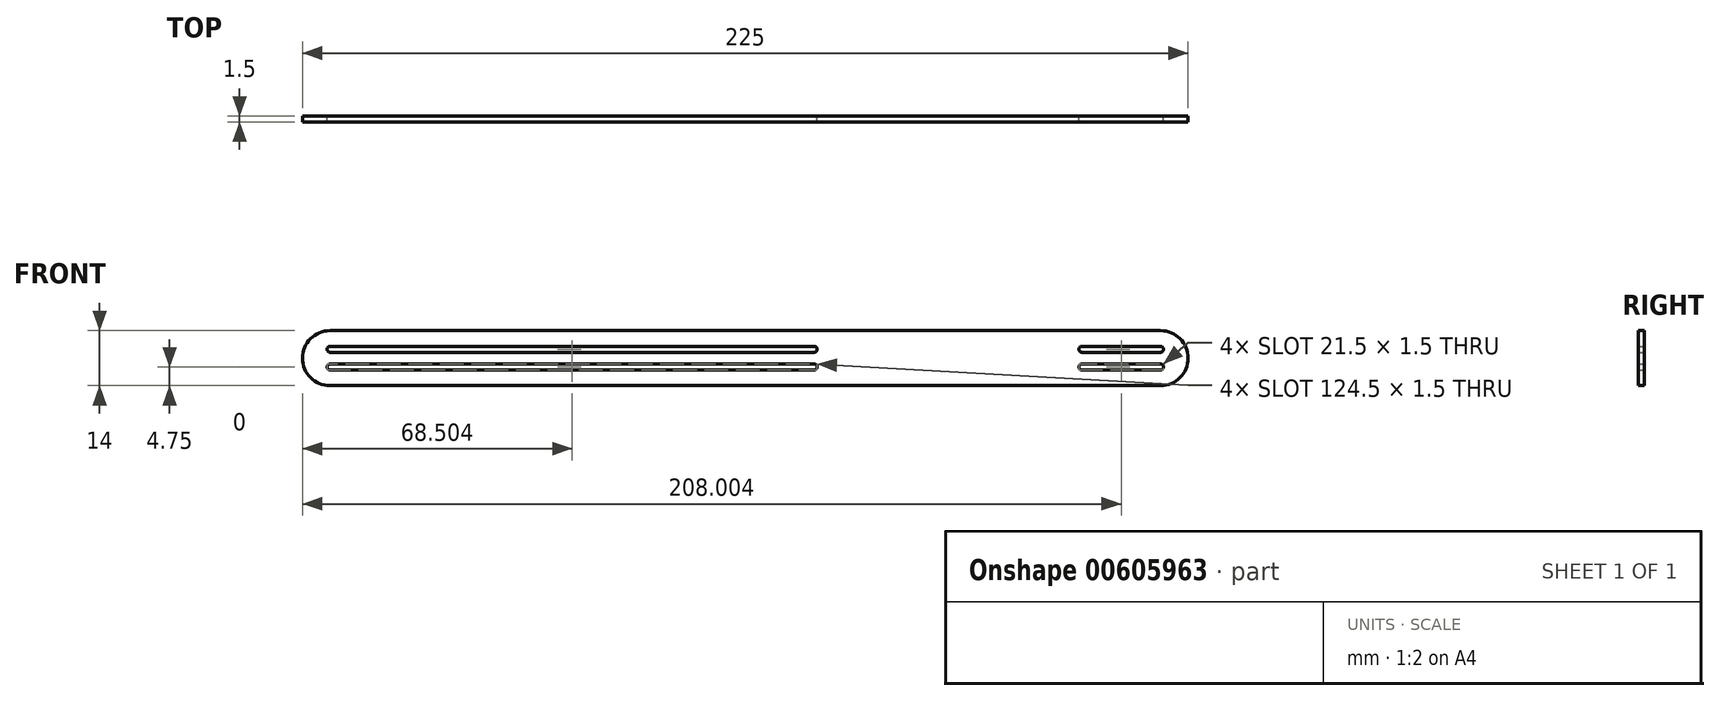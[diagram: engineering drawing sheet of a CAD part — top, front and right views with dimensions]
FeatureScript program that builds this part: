
annotation { "Feature Type Name" : "Feature", "Feature Type Description" : "" }
export const myFeature = defineFeature(function(context is Context, id is Id, definition is map)
    precondition{}
    {
        {
            var Q0;
            Q0=qCreatedBy(makeId("Front.planeOp"),FACE);
            var sketch = newSketch(context, id + "F0", { "sketchPlane" : qUnion([Q0])});
            skLineSegment(sketch, "E0.bottom", {"start": v(-136.23, 21.39) * mm, "end": v(74.77, 21.39) * mm});
            skLineSegment(sketch, "E0.top", {"start": v(-136.23, 7.39) * mm, "end": v(74.77, 7.39) * mm});
            skLineSegment(sketch, "E0.left", {"start": v(-136.23, 21.39) * mm, "end": v(-136.23, 7.39) * mm, "construction": true});
            skLineSegment(sketch, "E0.right", {"start": v(74.77, 21.39) * mm, "end": v(74.77, 7.39) * mm, "construction": true});
            skLineSegment(sketch, "E1", {"start": v(-136.23, 16.64) * mm, "end": v(-13.23, 16.64) * mm, "construction": true});
            skLineSegment(sketch, "E2", {"start": v(-136.23, 12.14) * mm, "end": v(-13.23, 12.14) * mm, "construction": true});
            skArc(sketch, "E3.0.startCap", {"start": v(-136.23, 15.89) * mm, "mid": v(-136.98, 16.64) * mm, "end": v(-136.23, 17.39) * mm});
            skArc(sketch, "E3.0.endCap", {"start": v(-13.23, 17.39) * mm, "mid": v(-12.48, 16.64) * mm, "end": v(-13.23, 15.89) * mm});
            skLineSegment(sketch, "E3.0.left", {"start": v(-136.23, 17.39) * mm, "end": v(-13.23, 17.39) * mm});
            skLineSegment(sketch, "E3.0.right", {"start": v(-136.23, 15.89) * mm, "end": v(-13.23, 15.89) * mm});
            skArc(sketch, "E4", {"start": v(-136.23, 21.39) * mm, "mid": v(-141.21, 19.3) * mm, "end": v(-143.23, 14.29) * mm});
            skArc(sketch, "E5", {"start": v(74.77, 21.39) * mm, "mid": v(79.8, 19.27) * mm, "end": v(81.77, 14.2) * mm});
            skArc(sketch, "E6.0.startCap", {"start": v(-136.23, 11.39) * mm, "mid": v(-136.98, 12.14) * mm, "end": v(-136.23, 12.89) * mm});
            skArc(sketch, "E6.0.endCap", {"start": v(-13.23, 12.89) * mm, "mid": v(-12.48, 12.14) * mm, "end": v(-13.23, 11.39) * mm});
            skLineSegment(sketch, "E6.0.left", {"start": v(-136.23, 12.89) * mm, "end": v(-13.23, 12.89) * mm});
            skLineSegment(sketch, "E6.0.right", {"start": v(-136.23, 11.39) * mm, "end": v(-13.23, 11.39) * mm});
            skLineSegment(sketch, "E7", {"start": v(74.77, 16.64) * mm, "end": v(54.77, 16.64) * mm, "construction": true});
            skLineSegment(sketch, "E8", {"start": v(74.77, 12.14) * mm, "end": v(54.77, 12.14) * mm, "construction": true});
            skArc(sketch, "E9.0.startCap", {"start": v(74.77, 12.89) * mm, "mid": v(75.52, 12.14) * mm, "end": v(74.77, 11.39) * mm});
            skArc(sketch, "E9.0.endCap", {"start": v(54.77, 11.39) * mm, "mid": v(54.02, 12.14) * mm, "end": v(54.77, 12.89) * mm});
            skLineSegment(sketch, "E9.0.left", {"start": v(74.77, 11.39) * mm, "end": v(54.77, 11.39) * mm});
            skLineSegment(sketch, "E9.0.right", {"start": v(74.77, 12.89) * mm, "end": v(54.77, 12.89) * mm});
            skArc(sketch, "E9.1.startCap", {"start": v(74.77, 17.39) * mm, "mid": v(75.52, 16.64) * mm, "end": v(74.77, 15.89) * mm});
            skArc(sketch, "E9.1.endCap", {"start": v(54.77, 15.89) * mm, "mid": v(54.02, 16.64) * mm, "end": v(54.77, 17.39) * mm});
            skLineSegment(sketch, "E9.1.left", {"start": v(74.77, 15.89) * mm, "end": v(54.77, 15.89) * mm});
            skLineSegment(sketch, "E9.1.right", {"start": v(74.77, 17.39) * mm, "end": v(54.77, 17.39) * mm});
            skLineSegment(sketch, "E10", {"start": v(-97.23, -33.2) * mm, "end": v(73.77, -33.2) * mm, "construction": true});
            skArc(sketch, "E11.0.startCap", {"start": v(-97.23, -41.2) * mm, "mid": v(-102.9, -38.83) * mm, "end": v(-105.23, -33.14) * mm});
            skArc(sketch, "E11.0.endCap", {"start": v(73.77, -25.2) * mm, "mid": v(79.34, -27.45) * mm, "end": v(81.77, -32.94) * mm});
            skLineSegment(sketch, "E11.0.left", {"start": v(-97.23, -25.2) * mm, "end": v(73.77, -25.2) * mm});
            skLineSegment(sketch, "E11.0.right", {"start": v(-97.23, -41.2) * mm, "end": v(73.77, -41.2) * mm});
            skLineSegment(sketch, "E12", {"start": v(-97.23, -25.2) * mm, "end": v(-97.23, -41.2) * mm, "construction": true});
            skLineSegment(sketch, "E13", {"start": v(73.77, -25.2) * mm, "end": v(73.77, -41.2) * mm, "construction": true});
            skLineSegment(sketch, "E14", {"start": v(-97.23, -36.44) * mm, "end": v(-17.23, -36.44) * mm, "construction": true});
            skLineSegment(sketch, "E15", {"start": v(-97.23, -29.94) * mm, "end": v(-17.23, -29.94) * mm, "construction": true});
            skLineSegment(sketch, "E16", {"start": v(73.77, -36.44) * mm, "end": v(53.77, -36.44) * mm, "construction": true});
            skLineSegment(sketch, "E17", {"start": v(73.77, -29.99) * mm, "end": v(53.77, -29.99) * mm, "construction": true});
            skArc(sketch, "E18.0.startCap", {"start": v(-97.23, -37.2) * mm, "mid": v(-97.98, -36.44) * mm, "end": v(-97.23, -35.7) * mm});
            skArc(sketch, "E18.0.endCap", {"start": v(-17.23, -35.7) * mm, "mid": v(-16.48, -36.44) * mm, "end": v(-17.23, -37.2) * mm});
            skLineSegment(sketch, "E18.0.left", {"start": v(-97.23, -35.7) * mm, "end": v(-17.23, -35.7) * mm});
            skLineSegment(sketch, "E18.0.right", {"start": v(-97.23, -37.2) * mm, "end": v(-17.23, -37.2) * mm});
            skArc(sketch, "E18.1.startCap", {"start": v(-97.23, -30.7) * mm, "mid": v(-97.98, -29.94) * mm, "end": v(-97.23, -29.2) * mm});
            skArc(sketch, "E18.1.endCap", {"start": v(-17.23, -29.2) * mm, "mid": v(-16.48, -29.94) * mm, "end": v(-17.23, -30.7) * mm});
            skLineSegment(sketch, "E18.1.left", {"start": v(-97.23, -29.2) * mm, "end": v(-17.23, -29.2) * mm});
            skLineSegment(sketch, "E18.1.right", {"start": v(-97.23, -30.7) * mm, "end": v(-17.23, -30.7) * mm});
            skArc(sketch, "E18.2.startCap", {"start": v(73.77, -29.24) * mm, "mid": v(74.52, -29.99) * mm, "end": v(73.77, -30.74) * mm});
            skArc(sketch, "E18.2.endCap", {"start": v(53.77, -30.74) * mm, "mid": v(53.02, -29.99) * mm, "end": v(53.77, -29.24) * mm});
            skLineSegment(sketch, "E18.2.left", {"start": v(73.77, -30.74) * mm, "end": v(53.77, -30.74) * mm});
            skLineSegment(sketch, "E18.2.right", {"start": v(73.77, -29.24) * mm, "end": v(53.77, -29.24) * mm});
            skArc(sketch, "E18.3.startCap", {"start": v(73.77, -35.7) * mm, "mid": v(74.52, -36.44) * mm, "end": v(73.77, -37.2) * mm});
            skArc(sketch, "E18.3.endCap", {"start": v(53.77, -37.2) * mm, "mid": v(53.02, -36.44) * mm, "end": v(53.77, -35.7) * mm});
            skLineSegment(sketch, "E18.3.left", {"start": v(73.77, -37.2) * mm, "end": v(53.77, -37.2) * mm});
            skLineSegment(sketch, "E18.3.right", {"start": v(73.77, -35.7) * mm, "end": v(53.77, -35.7) * mm});
            skPoint(sketch, "E19", {"position": v(81.77, 14.39) * mm});
            skPoint(sketch, "E20", {"position": v(81.77, -33.2) * mm});
            skPoint(sketch, "E21", {"position": v(-105.23, -33.2) * mm});
            skPoint(sketch, "E22", {"position": v(-143.23, 14.39) * mm});
            skArc(sketch, "E23", {"start": v(-105.23, -33.14) * mm, "mid": v(-102.86, -27.52) * mm, "end": v(-97.23, -25.2) * mm});
            skArc(sketch, "E24", {"start": v(-143.23, 14.29) * mm, "mid": v(-141.14, 9.4) * mm, "end": v(-136.23, 7.39) * mm});
            skArc(sketch, "E25", {"start": v(81.77, -32.94) * mm, "mid": v(79.52, -38.76) * mm, "end": v(73.77, -41.2) * mm});
            skArc(sketch, "E26", {"start": v(81.77, 14.2) * mm, "mid": v(79.65, 9.37) * mm, "end": v(74.77, 7.39) * mm});
            skLineSegment(sketch, "E27", {"start": v(-143.23, 14.29) * mm, "end": v(81.77, 14.39) * mm, "construction": true});
            skLineSegment(sketch, "E28", {"start": v(-105.23, -33.14) * mm, "end": v(81.77, -33.2) * mm, "construction": true});
            skLineSegment(sketch, "E29", {"start": v(81.77, 14.39) * mm, "end": v(81.77, -33.2) * mm, "construction": true});
            skSolve(sketch);
        }
        {
            var Q0;
            Q0=makeQuery(id+"F0.imprint","IMPRINT",FACE,{"disambiguationData":[TD([[makeQuery(id+"F0.imprint","IMPRINT",EDGE,{"derivedFrom":sQuery(id+"F0.wireOp",EDGE,"E0.bottom")}),-1.0]])]});
            var Q1;
            Q1=makeQuery(id+"F0.imprint","IMPRINT",FACE,{"disambiguationData":[TD([[makeQuery(id+"F0.imprint","IMPRINT",EDGE,{"derivedFrom":sQuery(id+"F0.wireOp",EDGE,"E11.0.startCap")}),-1.0]])]});
            extrude(context, id + "F1", {"entities" : qUnion([Q0, Q1]), "depth" : 1.5 * mm, "offsetDistance" : 25 * mm});
        }
    });
